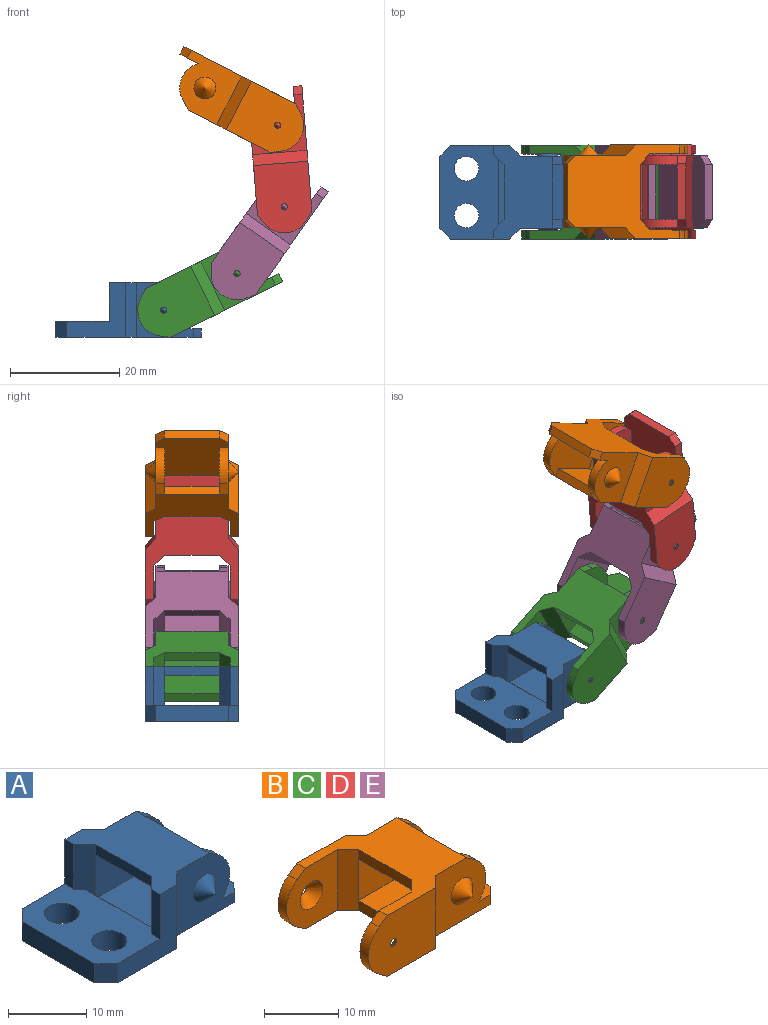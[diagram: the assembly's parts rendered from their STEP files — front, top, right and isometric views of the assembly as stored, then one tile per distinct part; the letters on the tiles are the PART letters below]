
ASSEMBLY  parts=5 mates=4
PART A: 34 faces, bbox 26.6x17.2x10 mm
  f0: plane 10.77x10mm, normal (0,-1,0), area 53.3mm2, adj f7,f8,f9,f24,f26,f29
  f1: plane 12.6x8.4mm, normal (0,1,0), area 84.3mm2, adj f2,f5,f10,f11,f20,f22,f27
  f2: plane 8x2mm, normal (-0.71,0.71,0), area 20.5mm2, adj f1,f7,f21,f24,f26,f27
  f3: plane 12.6x8.4mm, normal (0,-1,0), area 84.3mm2, adj f4,f5,f16,f17,f20,f22,f27
  f4: plane 8x2mm, normal (-0.71,-0.71,0), area 20.5mm2, adj f3,f7,f21,f24,f25,f27
  f5: plane 14.48x13.2mm, normal (0,0,1), area 154.6mm2, adj f1,f3,f6,f10,f13,f16,f19,f27
  f6: plane 10.38x10mm, normal (0,-1,0), area 77.4mm2, adj f5,f7,f8,f9,f10,f11,f12,f33
  f7: plane 17.2x10.88mm, normal (0,0,1), area 135.6mm2, adj f0,f2,f4,f6,f9,f11,f13,f14
  f8: plane 26.64x17.2mm, normal (0,0,-1), area 368.7mm2, adj f0,f6,f9,f13,f14,f15,f19,f23
  f9: plane 10x2mm, normal (0.71,-0.71,0), area 28.3mm2, adj f0,f6,f7,f8
  f10: cylinder r=4.6mm len=7.17mm, axis (0,-1,0), area 13.2mm2, adj f1,f5,f6,f11
  f11: plane 1.76x1.6mm, normal (0.57,0,0.82), area 3.4mm2, adj f1,f6,f7,f10
  f12: cone r=2mm half-angle=45deg, axis (0,1,0), area 17.8mm2, adj f6
  f13: plane 10.38x10mm, normal (0,1,0), area 77.4mm2, adj f5,f7,f8,f15,f16,f17,f18,f32
  f14: plane 10.77x10mm, normal (0,1,0), area 53.3mm2, adj f7,f8,f15,f24,f25,f28
  f15: plane 10x2mm, normal (0.71,0.71,0), area 28.3mm2, adj f7,f8,f13,f14
  f16: cylinder r=4.6mm len=7.17mm, axis (0,1,0), area 13.2mm2, adj f3,f5,f13,f17
  f17: plane 1.76x1.6mm, normal (0.57,0,0.82), area 3.4mm2, adj f3,f7,f13,f16
  f18: cone r=2mm half-angle=45deg, axis (0,-1,0), area 17.8mm2, adj f13
  f19: plane 10.2x1.6mm, normal (1,0,0), area 16.3mm2, adj f5,f8,f32,f33
  f20: plane 10x1.6mm, normal (1,0,0), area 16mm2, adj f1,f3,f7,f22
  f21: plane 10x1.6mm, normal (-1,0,0), area 16mm2, adj f2,f4,f7,f22
  f22: plane 10x8.88mm, normal (0,0,-1), area 88.8mm2, adj f1,f3,f20,f21
  f23: plane 13.2x3mm, normal (-1,0,0), area 39.6mm2, adj f8,f24,f28,f29
  f24: plane 17.2x10.77mm, normal (0,0,1), area 145.2mm2, adj f0,f2,f4,f14,f23,f25,f26,f27
  f25: plane 7x1.6mm, normal (-1,0,0), area 11.2mm2, adj f4,f7,f14,f24
  f26: plane 7x1.6mm, normal (-1,0,0), area 11.2mm2, adj f0,f2,f7,f24
  f27: plane 12x1.4mm, normal (0.71,0,0.71), area 21.2mm2, adj f1,f2,f3,f4,f5,f24
  f28: plane 3x2mm, normal (-0.71,0.71,0), area 8.5mm2, adj f8,f14,f23,f24
  f29: plane 3x2mm, normal (-0.71,-0.71,0), area 8.5mm2, adj f0,f8,f23,f24
  f30: cylinder r=2.25mm len=4.5mm, axis (0,0,1), area 42.4mm2, adj f8,f24
  f31: cylinder r=2.25mm len=4.5mm, axis (0,0,1), area 42.4mm2, adj f8,f24
  f32: plane 1.6x1.5mm, normal (0.71,0.71,0), area 3.4mm2, adj f5,f8,f13,f19
  f33: plane 1.6x1.5mm, normal (0.71,-0.71,0), area 3.4mm2, adj f5,f6,f8,f19
PART B: 36 faces, bbox 26.6x17.2x10 mm
  f0: plane 12.6x8.4mm, normal (0,1,0), area 84.4mm2, adj f7,f9,f10,f30,f31,f33
  f1: plane 10.38x10mm, normal (0,-1,0), area 77.4mm2, adj f4,f5,f6,f9,f10,f14,f30,f35
  f2: plane 10x9.77mm, normal (0,1,0), area 72mm2, adj f4,f5,f7,f8,f11,f12,f13
  f3: plane 12.77x10mm, normal (0,-1,0), area 115.7mm2, adj f4,f5,f6,f8,f11,f12,f13
  f4: plane 17.2x17.05mm, normal (0,0,1), area 155.3mm2, adj f1,f2,f3,f6,f7,f10,f13,f16
  f5: plane 23.05x17.2mm, normal (0,0,-1), area 232.3mm2, adj f1,f2,f3,f6,f7,f12,f16,f17
  f6: plane 10x2mm, normal (0.71,-0.71,0), area 28.3mm2, adj f1,f3,f4,f5
  f7: plane 10x2mm, normal (-0.71,0.71,0), area 28.3mm2, adj f0,f2,f4,f5,f28,f32
  f8: cone r=2.17mm half-angle=45deg, axis (0,1,0), area 19.4mm2, adj f2,f3
  f9: cylinder r=4.6mm len=7.17mm, axis (0,-1,0), area 13.2mm2, adj f0,f1,f10,f30
  f10: plane 1.76x1.6mm, normal (0.57,0,0.82), area 3.4mm2, adj f0,f1,f4,f9
  f11: cylinder r=4.77mm len=7.81mm, axis (0,-1,0), area 14.6mm2, adj f2,f3,f12,f13
  f12: plane 1.6x1.57mm, normal (-0.57,0,-0.82), area 3.1mm2, adj f2,f3,f5,f11
  f13: plane 1.6x1.57mm, normal (-0.57,0,0.82), area 3.1mm2, adj f2,f3,f4,f11
  f14: cone r=2mm half-angle=45deg, axis (0,1,0), area 17.8mm2, adj f1
  f15: plane 12.6x8.4mm, normal (0,-1,0), area 84.4mm2, adj f20,f22,f23,f30,f31,f33
  f16: plane 10.38x10mm, normal (0,1,0), area 77.4mm2, adj f4,f5,f19,f22,f23,f27,f30,f34
  f17: plane 10x9.77mm, normal (0,-1,0), area 72mm2, adj f4,f5,f20,f21,f24,f25,f26
  f18: plane 12.77x10mm, normal (0,1,0), area 115.7mm2, adj f4,f5,f19,f21,f24,f25,f26
  f19: plane 10x2mm, normal (0.71,0.71,0), area 28.3mm2, adj f4,f5,f16,f18
  f20: plane 10x2mm, normal (-0.71,-0.71,0), area 28.3mm2, adj f4,f5,f15,f17,f28,f32
  f21: cone r=2.17mm half-angle=45deg, axis (0,-1,0), area 19.4mm2, adj f17,f18
  f22: cylinder r=4.6mm len=7.17mm, axis (0,1,0), area 13.2mm2, adj f15,f16,f23,f30
  f23: plane 1.76x1.6mm, normal (0.57,0,0.82), area 3.4mm2, adj f4,f15,f16,f22
  f24: cylinder r=4.77mm len=7.81mm, axis (0,1,0), area 14.6mm2, adj f17,f18,f25,f26
  f25: plane 1.6x1.57mm, normal (-0.57,0,-0.82), area 3.1mm2, adj f5,f17,f18,f24
  f26: plane 1.6x1.57mm, normal (-0.57,0,0.82), area 3.1mm2, adj f4,f17,f18,f24
  f27: cone r=2mm half-angle=45deg, axis (0,-1,0), area 17.8mm2, adj f16
  f28: plane 10x1.6mm, normal (-1,0,0), area 16mm2, adj f5,f7,f20,f30
  f29: plane 10.2x1.6mm, normal (1,0,0), area 16.3mm2, adj f5,f30,f34,f35
  f30: plane 14.88x13.2mm, normal (0,0,1), area 158.6mm2, adj f0,f1,f9,f15,f16,f22,f28,f29
  f31: plane 10x1.6mm, normal (1,0,0), area 16mm2, adj f0,f4,f15,f33
  f32: plane 10x1.6mm, normal (-1,0,0), area 16mm2, adj f4,f7,f20,f33
  f33: plane 10x8.88mm, normal (0,0,-1), area 88.8mm2, adj f0,f15,f31,f32
  f34: plane 1.6x1.5mm, normal (0.71,0.71,0), area 3.4mm2, adj f5,f16,f29,f30
  f35: plane 1.6x1.5mm, normal (0.71,-0.71,0), area 3.4mm2, adj f1,f5,f29,f30
PART C: same geometry as B
PART D: same geometry as B
PART E: same geometry as B
PLACE A at identity fixed
PLACE B rot(axis=(0,-1,0),152.8deg) t=(26.49,0,32.52)mm
PLACE C rot(axis=(0,-1,0),26.4deg) t=(0.31,0,-1.32)mm
PLACE D rot(axis=(0,-1,0),94.6deg) t=(25.29,0,15.97)mm
PLACE E rot(axis=(0,-1,0),54.8deg) t=(14.69,0,4.25)mm
MATE revolute D.f21 <-> E.f27  axis (0,-1,0) through (25.05,-20.77,18.93)mm
MATE revolute B.f21 <-> D.f27  axis (0,-1,0) through (23.85,-20.77,33.88)mm
MATE revolute E.f21 <-> C.f27  axis (0,-1,0) through (16.4,-20.77,6.67)mm
MATE revolute C.f21 <-> A.f18  axis (0,-1,0) through (2.97,-20.77,0)mm
